# Revit family: Sanitary_Bidets_DURAVIT-AG_D-Neo-Floor-mounted-bidet-White-High-Gloss-650mm-229410
name_source: partatom
category: Plumbing Fixtures
revit_build: Autodesk Revit 2018 (Build: 20190510_1515(x64)
units: mm (PartAtom-declared; Revit-internal decimal feet)

## family parameters
Cut with Voids When Loaded = No
Host = Face
OmniClass Number = 23.31.23.00
OmniClass Title = Bidets
Part Type = Normal
Room Calculation Point = No
Round Connector Dimension = Use Diameter
Shared = No

## types (2) — shared parameters
BIMobject category = Bidets
Connector Description = Water outlet
Connector Description 2 = Water inlet
Default Elevation = 1219 mm
Design country = Germany
Details material = Duravit - Metal - 10 - Chrome
ETIM classification = EC010126 | Bidet
Edition number = 1
IFC Classification = Sanitary Terminal
Inlet Diameter = 35  [stored 0.114829 ft]
Installation instructions = https://duravit-public-assets.s3.eu-central-1.amazonaws.com
Manufacturer = Duravit
Manufacturer name = DURAVIT AG
Masterformat 2014 Code = 22 41 13.19
Masterformat 2014 Description = Residential Bidets
Material main = Ceramics
Model = D-Neo Floorstanding bidet White High Gloss 650 mm - 229410
OmniClass Code = 23-31 23 00
OmniClass Description = Bidets
Outlet Diameter = 32  [stored 0.104987 ft]
Product Guid = 9cf06833-2df3-4183-8675-f25ed285c3c2
Product SKU = d-neo-floor-mounted-bidet-229410
Product certification = http://pro.duravit.com
Product data url = https://bimobject.com
Product family = Bidets
Product group = Floorstanding bidet
Product name = D-Neo Floorstanding bidet White High Gloss 650 mm - 229410
Product url = https://duravit-public-assets.s3.eu-central-1.amazonaws.com
QR code = https://bimobject.com
Technical description = http://pro.duravit.com
UNSPSC Code = 30181502
URL = https://www.duravit.com
Uniclass 2015 Code = Pr_40_20_06_11
Uniclass 2015 Name = Bidets
Uniformat II Code = D2010
Uniformat II Description = Plumbing Fixtures
Weight Net (Kg) = 35,7
Youtube clip = http://pro.duravit.com

## per-type parameters (varying)
| type | Description | Main material |
| 00 - White Alpin | Duravit D-Neo Floorstanding bidet, 650 mm White High Gloss, Tap hole platform, Number of faucet holes per wash area: 1, Overflow - 2294100000 | Duravit - Ceramic - 00 - White Alpin |
| 00 - White Alpin WonderGliss | Duravit D-Neo Floorstanding bidet, 650 mm White High Gloss, Tap hole platform, Number of faucet holes per wash area: 1, Overflow, WonderGliss - 22941000001 | Duravit - Ceramic - 00 - White Alpin WonderGliss |

note: [stored X ft] marks values corroborated as IEEE doubles in the binary element streams (Revit-internal decimal feet)

## geometry (parser evidence)
native form markers: Sweep x3
no freeform markers — native parametric forms only
